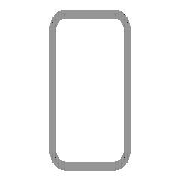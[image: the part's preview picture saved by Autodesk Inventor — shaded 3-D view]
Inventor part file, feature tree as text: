
AUTODESK INVENTOR PART (.ipt)
format: ipt  version: 2025 (Build 290162010, 162A)  size: 129,024 bytes
history: native  units: mm (DEFAULTED — no unit token found)
features: other x3, sketch x1, plane x1
ambient origin geometry x8: Origin, YZ Plane, XZ Plane, XY Plane, X Axis, Y Axis, Z Axis, Center Point
bodies: Solid1 (feature_tree), Body (feature_tree)
feature tree (5):
  other  "Driven Length"
  other  "Start plane"
  other  "End plane"
  sketch  "Sketch3"  dims[d3=1380.0mm d4=0.0mm d7=6.0mm d9=40.0mm d11=60.0mm d12=3.0mm d13=-0.0mm d14=1380.0mm d15=20.0mm d16=30.0mm d17=90.0deg d18=1380.0mm]
  plane  "Work Plane3"
